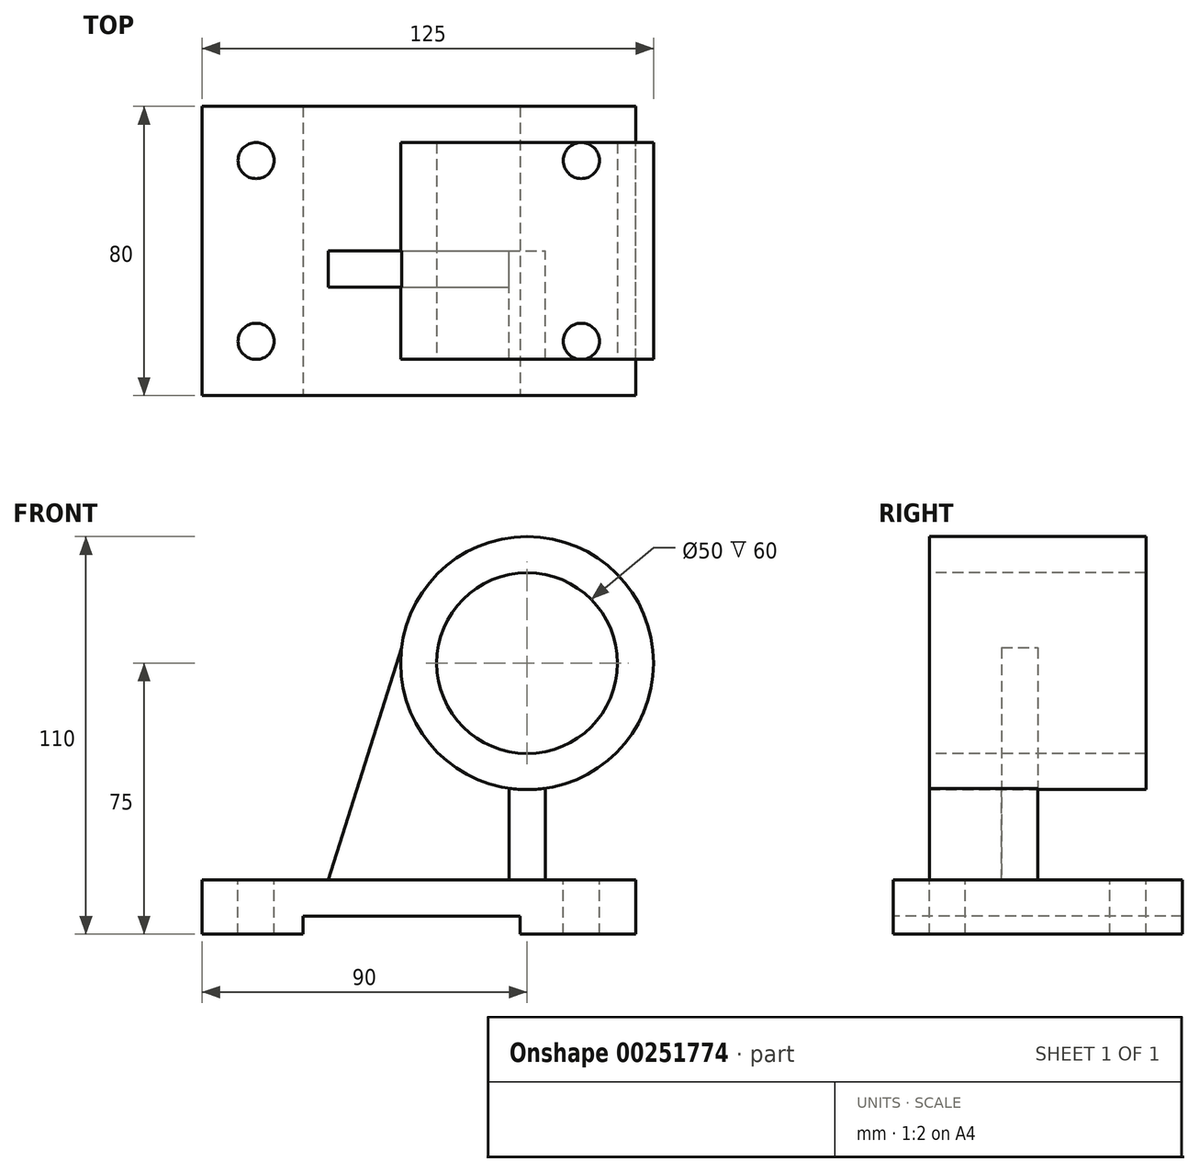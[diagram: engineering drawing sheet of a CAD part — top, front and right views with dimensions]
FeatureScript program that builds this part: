
annotation { "Feature Type Name" : "Feature", "Feature Type Description" : "" }
export const myFeature = defineFeature(function(context is Context, id is Id, definition is map)
    precondition{}
    {
        {
            var Q0;
            Q0=qCreatedBy(makeId("Front.planeOp"),FACE);
            var sketch = newSketch(context, id + "F0", { "sketchPlane" : qUnion([Q0])});
            skLineSegment(sketch, "E0.bottom", {"start": v(-60, 7.5) * mm, "end": v(60, 7.5) * mm});
            skLineSegment(sketch, "E0.top", {"start": v(-60, -7.5) * mm, "end": v(60, -7.5) * mm});
            skLineSegment(sketch, "E0.left", {"start": v(-60, 7.5) * mm, "end": v(-60, -7.5) * mm});
            skLineSegment(sketch, "E0.right", {"start": v(60, 7.5) * mm, "end": v(60, -7.5) * mm});
            skPoint(sketch, "E0.middle", {"position": v(0, 0) * mm});
            skSolve(sketch);
        }
        {
            var Q0;
            Q0 = qSketchRegion(id + "F0", true);
            extrude(context, id + "F1", {"entities" : qUnion([Q0]), "endBound" : BoundingType.SYMMETRIC, "depth" : 80 * mm});
        }
        {
            var Q0;
            Q0=makeQuery(id+"F1.opExtrude","CAP_FACE",FACE,{"disambiguationData":[OSD([sQuery(id+"F0.wireOp",EDGE,"E0.bottom"),sQuery(id+"F0.wireOp",EDGE,"E0.top"),sQuery(id+"F0.wireOp",EDGE,"E0.left"),sQuery(id+"F0.wireOp",EDGE,"E0.right")])],"isStart":false});
            var sketch = newSketch(context, id + "F2", { "sketchPlane" : qUnion([Q0])});
            skLineSegment(sketch, "E1.bottom", {"start": v(-32, -7.5) * mm, "end": v(28, -7.5) * mm});
            skLineSegment(sketch, "E1.top", {"start": v(-32, -2.5) * mm, "end": v(28, -2.5) * mm});
            skLineSegment(sketch, "E1.left", {"start": v(-32, -7.5) * mm, "end": v(-32, -2.5) * mm});
            skLineSegment(sketch, "E1.right", {"start": v(28, -7.5) * mm, "end": v(28, -2.5) * mm});
            skSolve(sketch);
        }
        {
            var Q0;
            Q0 = qSketchRegion(id + "F2", true);
            extrude(context, id + "F3", {"entities" : qUnion([Q0]), "operationType" : NewBodyOperationType.REMOVE, "endBound" : BoundingType.THROUGH_ALL, "oppositeDirection" : true, "depth" : 25 * mm});
        }
        {
            var Q0;
            Q0=makeQuery(id+"F1.opExtrude","SWEPT_FACE",FACE,{"disambiguationData":[OSD([sQuery(id+"F0.wireOp",EDGE,"E0.bottom")])]});
            var sketch = newSketch(context, id + "F4", { "sketchPlane" : qUnion([Q0])});
            skCircle(sketch, "E2", {"center": v(-45, 25) * mm, "radius": 5 * mm});
            skCircle(sketch, "E3", {"center": v(-45, -25) * mm, "radius": 5 * mm});
            skCircle(sketch, "E4", {"center": v(45, -25) * mm, "radius": 5 * mm});
            skCircle(sketch, "E5", {"center": v(45, 25) * mm, "radius": 5 * mm});
            skSolve(sketch);
        }
        {
            var Q0;
            Q0 = qSketchRegion(id + "F4", true);
            extrude(context, id + "F5", {"entities" : qUnion([Q0]), "operationType" : NewBodyOperationType.REMOVE, "endBound" : BoundingType.THROUGH_ALL, "oppositeDirection" : true, "depth" : 25 * mm});
        }
        {
            var Q0;
            Q0=qCreatedBy(makeId("Front.planeOp"),FACE);
            var sketch = newSketch(context, id + "F6", { "sketchPlane" : qUnion([Q0])});
            skCircle(sketch, "E6", {"center": v(30, 67.5) * mm, "radius": 25 * mm});
            skCircle(sketch, "E7", {"center": v(30, 67.5) * mm, "radius": 35 * mm});
            skPoint(sketch, "E8.orphan", {"position": v(30, -69.01) * mm});
            skSolve(sketch);
        }
        {
            var Q0;
            Q0 = qSketchRegion(id + "F6", true);
            extrude(context, id + "F7", {"entities" : qUnion([Q0]), "endBound" : BoundingType.SYMMETRIC, "oppositeDirection" : true, "depth" : 60 * mm});
        }
        {
            var Q0;
            Q0=qCreatedBy(makeId("Front.planeOp"),FACE);
            var sketch = newSketch(context, id + "F8", { "sketchPlane" : qUnion([Q0])});
            skArc(sketch, "E9.0", {"start": v(25, 32.86) * mm, "mid": v(30, 32.5) * mm, "end": v(35, 32.86) * mm});
            skLineSegment(sketch, "E10.0", {"start": v(25, 7.5) * mm, "end": v(35, 7.5) * mm});
            skLineSegment(sketch, "E11.bottom", {"start": v(35, 7.5) * mm, "end": v(25, 7.5) * mm});
            skLineSegment(sketch, "E11.left", {"start": v(35, 7.5) * mm, "end": v(35, 32.86) * mm});
            skLineSegment(sketch, "E11.right", {"start": v(25, 7.5) * mm, "end": v(25, 32.86) * mm});
            skPoint(sketch, "E11.middle", {"position": v(30, 32.5) * mm});
            skPoint(sketch, "E12.orphan", {"position": v(-60, 7.5) * mm});
            skPoint(sketch, "E13.orphan", {"position": v(60, 7.5) * mm});
            skPoint(sketch, "E11.top.end.orphan", {"position": v(25, 57.5) * mm});
            skPoint(sketch, "E11.top.start.orphan", {"position": v(35, 57.5) * mm});
            skSolve(sketch);
        }
        {
            var Q0;
            Q0 = qSketchRegion(id + "F8", true);
            extrude(context, id + "F9", {"entities" : qUnion([Q0]), "depth" : 30 * mm});
        }
        {
            var Q0;
            Q0=qCreatedBy(makeId("Front.planeOp"),FACE);
            var sketch = newSketch(context, id + "F10", { "sketchPlane" : qUnion([Q0])});
            skArc(sketch, "E14.0", {"start": v(-4.74, 71.74) * mm, "mid": v(2.2, 46.24) * mm, "end": v(25, 32.86) * mm});
            skLineSegment(sketch, "E15.0", {"start": v(-25, 7.5) * mm, "end": v(25, 7.5) * mm});
            skLineSegment(sketch, "E16.bottom", {"start": v(25, 7.5) * mm, "end": v(-25, 7.5) * mm});
            skLineSegment(sketch, "E16.left", {"start": v(25, 7.5) * mm, "end": v(25, 32.86) * mm});
            skPoint(sketch, "E17.orphan", {"position": v(-60, 7.5) * mm});
            skPoint(sketch, "E18.orphan", {"position": v(60, 7.5) * mm});
            skLineSegment(sketch, "E19", {"start": v(-4.74, 71.74) * mm, "end": v(-25, 7.5) * mm});
            skSolve(sketch);
        }
        {
            var Q0;
            Q0 = qSketchRegion(id + "F10", true);
            extrude(context, id + "F11", {"entities" : qUnion([Q0]), "depth" : 10 * mm});
        }
    });
